# Revit family: Lighting_Pendants_Zero_PXL_Pendant
name_source: partatom
category: Lighting Fixtures
units: mm (PartAtom-declared; Revit-internal decimal feet)

## family parameters
Always vertical = Yes
Cut with Voids When Loaded = No
Light Source = Yes
OmniClass Number = 23.80.70.00
OmniClass Title = Lighting
Part Type = Normal
Room Calculation Point = No
Round Connector Dimension = Use Diameter
Shared = No
Work Plane-Based = Yes

## types (2) — shared parameters
Accessories = Two piece ceiling rose (98899-1-01)
AssetType = Fixed
BIMObjectName = Lighting_Pendants_Zero_PXL_Pendant
Brand = Zero
Brand url = http://www.zero.se
Category = Pendant
Collection = PXL
Color Filter = 16777215
Design country = Sweden
Designer = Fredrik Mattson
Dimming = None
Dimming Lamp Color Temperature Shift = <None>
DurationUnit = Year
Edition number = 1
Emit Shape Visible in Rendering = No
Emit from Circle Diameter = 158 mm
Features = Terminal block 2x2,5mm2
Finish = Aluminum and steel, multicolour
HasProtectiveEarth = No
IP_Code = IP20
IfcExportAs = IfcLightFixtureType
IfcExportType = NOTDEFINED
LightFixtureMainMaterial = White Painted Metal RAL9006
LightFixtureMountingType = Suspended
LightFixturePlacingType = Ceiling
Manufacturer country = Sweden
Manufacturer name = ZERO
ManufacturerName = Zero
ManufacturerURL = https://www.zerolighting.com
Material = Aluminum, steel
Material main = Steel
NBSDescription = General purpose luminaires
NBSReference = 90-60-50/405
Name = Zero_PXL_Pendant
Nominal height = 395 mm  [stored 1.29593 ft]
Nominal width = 320 mm  [stored 1.04987 ft]
NominalCurrent = 0 A
NominalDiameter = 320 mm  [stored 1.04987 ft]
NominalFrequencyRange = 50 Hz
NominalLength = 320 mm  [stored 1.04987 ft]
NominalRadius = 160 mm
NominalVoltage = 230 V
NominalVoltageCalc = 0 V
NumberOfPoles = 1
PhaseAngle = 0.00°
Photometric Web File = PXL7770.IES
Product Guid = bb679aad-cfe1-4974-84b8-07f18c5aa7eb
Product SKU = Pxl_pendant
Product family = Pxl
Product group = Pendant
Revision = 5
Shape = Sculptured
Size = 320x320x395 mm
Tilt Angle = 90.00°
TotalWattage = 9 W
URL = https://www.zerolighting.com
Uniclass2 = Pr_70_70_49_86
Uniclass2015Description = Suspended luminaires
Uniclass2015Reference = Pr_70_70_48_86
UsageCurrent = 0 A
Version = 3
VersionDate = 31/08/2023
WarrantyDurationUnit = Year
Weight Net (Kg) = 2.2
zero-valued in all types: DefaultElevation, ElectricalDeviceNominalPower, MaintenanceFactor, NumberOfSources

## per-type parameters (varying)
| type | ArticleNumber | Color | LightFixtureQuaternaryMaterial | LightFixtureQuinaryMaterial | LightFixtureSecondaryMaterial | LightFixtureTertiaryMaterial | Manufacturer | Model | ModelNumber |
| E27 Multicolour | 7770-1-90 | Multicolour | Red Painted Metal RAL3028 | Yellow Painted Metal RAL1018 | Black Painted Metal RAL9005 | Blue Painted Metal RAL5012 | Zero | PXL small E27 Multicolour | 7770-1-90 |
| E27 White | 7770-1-01 | White | White Painted Metal RAL9006 | White Painted Metal RAL9006 | White Painted Metal RAL9006 | White Painted Metal RAL9006 |  | PXL small E27 White | 7770-1-01 |

note: [stored X ft] marks values corroborated as IEEE doubles in the binary element streams (Revit-internal decimal feet)

## geometry (parser evidence)
native form markers: Sweep x4
no freeform markers — native parametric forms only
